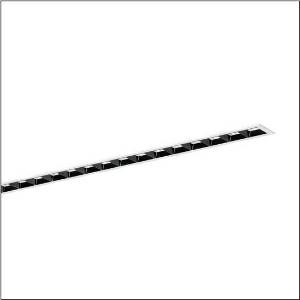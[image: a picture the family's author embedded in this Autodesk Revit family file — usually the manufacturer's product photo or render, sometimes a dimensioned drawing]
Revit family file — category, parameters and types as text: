
# Revit family: silica_r__21_51mx14dc3awb_1e66
name_source: partatom
category: Lighting Fixtures
units: mm (PartAtom-declared; Revit-internal decimal feet)

## family parameters
Cut with Voids When Loaded = No
Host = Face
Light Source = No
Part Type = Normal
Room Calculation Point = No
Round Connector Dimension = Use Diameter
Shared = No

## types (1)
- --- (1 x LED, 10800 lm, 79 W, 3000K)
    Apparent Load = 79 VA
    CIE Flux Codes = 74 94 99 100 100
    Color Rendering = 80
    Color Temperature = 3000K
    Default Elevation = 1800 mm
    Description = Silica® 21, office luminaire, primary light control with darklight reflector, of PMMA, black, light emission: direct distribution, primary light characteristic: asymmetric, installation type: recessed, LED, rated luminous flux: 10.800lm, luminous efficacy: 137lm/W, light colour: 830, colour temperature: 3000K, control gear: DALI 2, with terminal, 3+2-pole, max. 2.5mm², mains connection: 220..240V, AC, 50/60Hz, rated input power: 79W, luminaire housing, of aluminium, traffic white (RAL 9016), length: 3.028mm, width: 79mm, height: 53mm, protection rating (complete): IP20, insulation class (complete): insulation class I (protective earthing), certification: CE, ENEC, VDE, permissible operating ambient temperature: 0..+35°C, standard: EN 50419, packaging unit: 1 piece
    Height = 0 mm  [stored 0 ft]
    Lamp = 1 x LED
    Lamp Light Flux = 10800 lm
    Lamp Power = 79 W
    Lamp count = 1
    Length = 3027 mm
    Luminous efficacy = 137 lm/W
    Manufacturer = Siteco
    ModVariant = No
    Model = 51MX14DC3AWB
    Mounting Place = Ceiling
    Mounting Type = Recessed
    Number of Poles = 1
    OnlyDefault = Yes
    Power Factor = 1
    Product Name = Silica® 21
    Product group = office luminaire | ceiling recessed
    ProductGroupID = 400
    Protection Class = Protection class I
    Protection Degree = IP 20
    RLX_Detail_Level = 1
    RLX_Emergency_Light_Flux = 0 lm
    RLX_Emergency_Type = 0
    RLX_Emergency_Type_DB = No
    RlxData = <blob elided: 63377 chars, md5=05f1f4c3>
    Socket = socket
    Standby Power = 0 W
    System Light Flux = 10800 lm
    System Power = 79 W
    Type Comments = factory setting: luminous flux: 100 % | dim-lin: 254 | 448 mA
    Type Image = l_1335880.jpg
    URL = http://relux.com
    VarID = @adj_143841
    Voltage = 0 V
    Weight = 0.00 kg
    Width = 79 mm

note: [stored X ft] marks values corroborated as IEEE doubles in the binary element streams (Revit-internal decimal feet)

## geometry (parser evidence)
native form markers: Blend x4, Sweep x10
no freeform markers — native parametric forms only
